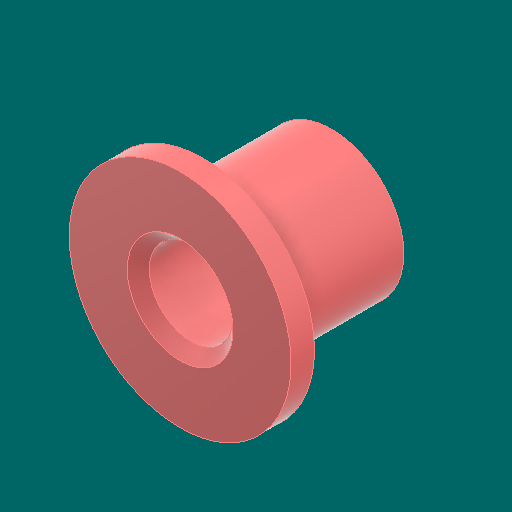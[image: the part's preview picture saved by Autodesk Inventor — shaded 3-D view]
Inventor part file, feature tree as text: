
AUTODESK INVENTOR PART (.ipt)
format: ipt  version: 2023.1 (Build 271208000, 208)  size: 121,856 bytes
history: native  units: in
note: dims shown in document units (in); Inventor stores cm internally (conversion verified against a paired STEP export)
features: other x3, sketch x2
ambient origin geometry x8: Origin, YZ Plane, XZ Plane, XY Plane, X Axis, Y Axis, Z Axis, Center Point
bodies: Solid1 (feature_tree)
feature tree (5):
  other  "bearingsleeve.ipt"
  other  "Solid1::bearingsleeve.ipt"
  other  "TaggingFeature1"
  sketch  "Sketch1"  dims[d0=0.3937in]
  sketch  "Sketch2"
